# Revit family: QF_MACOM_CH73C-N_G
name_source: partatom
category: Equipamento especial
units: mm (PartAtom-declared; Revit-internal decimal feet)

## family parameters
Com base no plano de trabalho = Não
Compartilhado = Não
Corte com vazios quando carregada = Não
Cota do conector redondo = Utilizar diâmetro
Número OmniClass = 23.40.40.14.17.14
Ponto de cálculo do ambiente = Não
Sempre na vertical = Sim
Tipo de parte = Normal
Título OmniClass = Hot Plates

## types (2) — shared parameters
Depth = 745,000 mm
Descrição = CHAPA 700HP MACOM 1080
Elevação padrão = 0,000 mm
Fabricante = MACOM
Gas Connection Height = 64,000 mm
Gas Pressure = 0,0 bar
Gas Size = 3/4"
Height = 337,000 mm
Plate Depth = 510,000 mm
Plate Width = 1075,000 mm
URL = https://www.acosmacom.com.br
Volume = 0,21 m³
Weight = 150,00 kg
Width = 1080,000 mm

## per-type parameters (varying)
| type | Gas Consumption GLP | Gas Consumption GN | Gas Input GLP | Gas Input GN |
| CH73C-N |  | 1,1 m³/h | 0 Btu/h | 10368 Kcal/h |
| CH73C-G | 0,90 Kg/h | 0,0 m³/h | 41140 Btu/h |  |

note: column(s) folded — value = type name in every type: Modelo

## geometry (parser evidence)
native form markers: Sweep x4
no freeform markers — native parametric forms only
